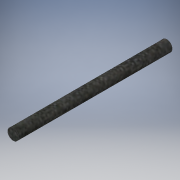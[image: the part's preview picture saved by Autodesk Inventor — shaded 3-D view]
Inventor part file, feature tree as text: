
AUTODESK INVENTOR PART (.ipt)
format: ipt  version: 2018 (Build 220112000, 112)  size: 97,280 bytes
history: native  units: mm
features: extrude x1, sketch x1
ambient origin geometry x8: Origin, YZ Plane, XZ Plane, XY Plane, X Axis, Y Axis, Z Axis, Center Point
bodies: Volumenkörper1 (feature_tree)
feature tree (2):
  extrude  "Extrusion1"  Depth=70.0mm TaperAngle=0.0deg
  sketch  "Skizze1"  dims[d0=5.0mm d1=70.0mm d2=0.0mm]
